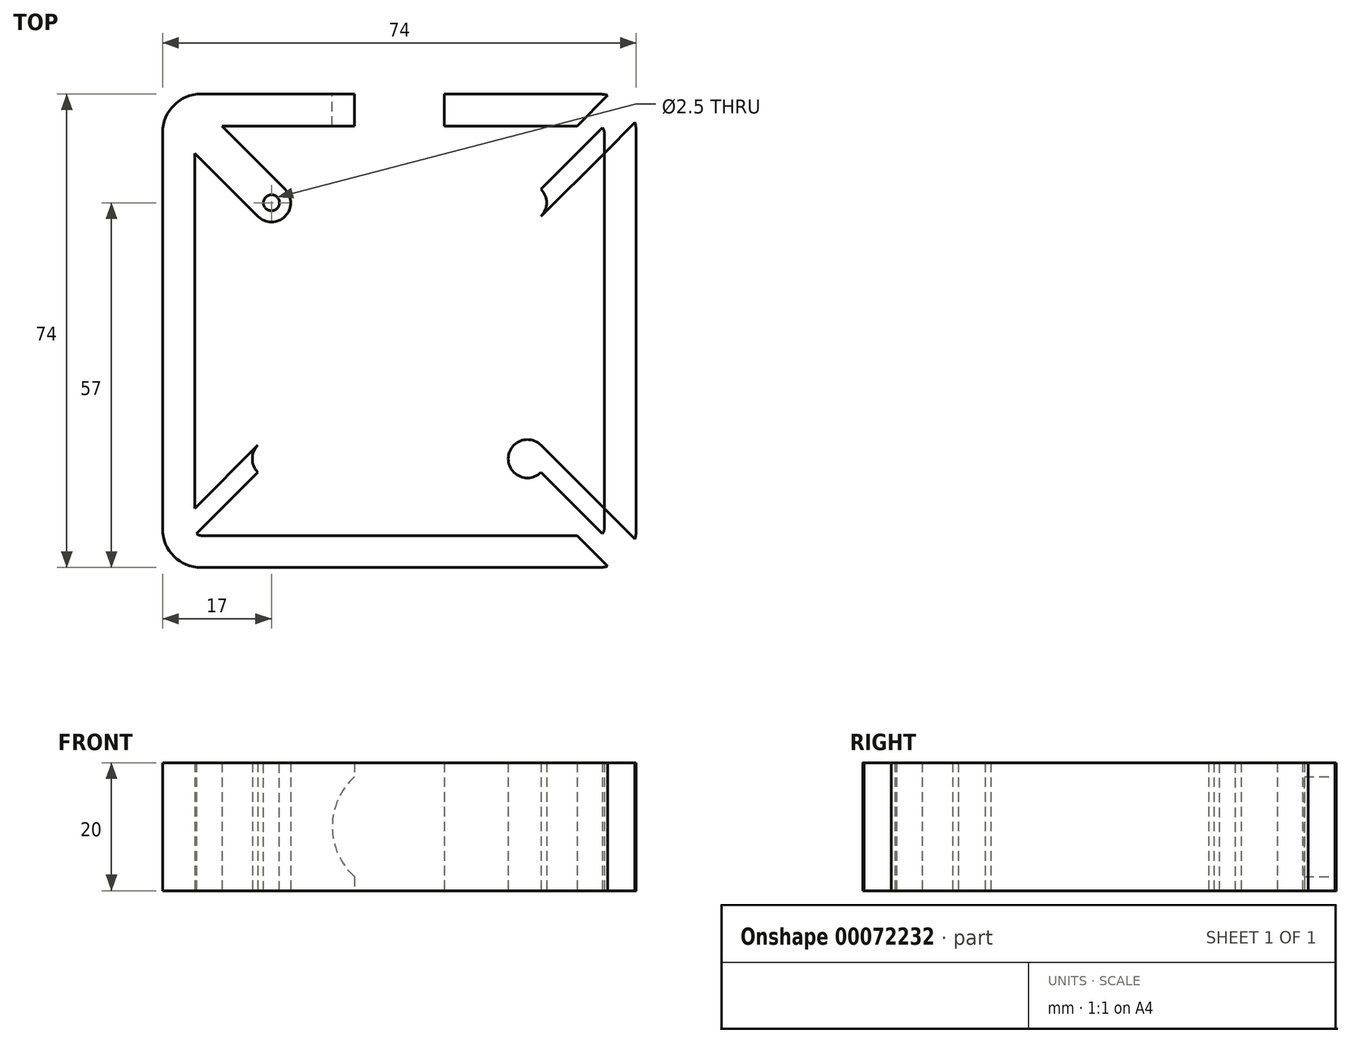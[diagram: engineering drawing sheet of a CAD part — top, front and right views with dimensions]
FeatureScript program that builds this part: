
annotation { "Feature Type Name" : "Feature", "Feature Type Description" : "" }
export const myFeature = defineFeature(function(context is Context, id is Id, definition is map)
    precondition{}
    {
        {
            var Q0;
            Q0=qCreatedBy(makeId("Top.planeOp"),FACE);
            var sketch = newSketch(context, id + "F0", { "sketchPlane" : qUnion([Q0])});
            skLineSegment(sketch, "E0.top", {"start": v(6, 74) * mm, "end": v(68, 74) * mm, "construction": true});
            skLineSegment(sketch, "E0.left", {"start": v(0, 6) * mm, "end": v(0, 68) * mm});
            skPoint(sketch, "E1.visualSharp", {"position": v(0, 74) * mm});
            skArc(sketch, "E1.filletArc", {"start": v(6, 74) * mm, "mid": v(1.76, 72.24) * mm, "end": v(0, 68) * mm});
            skPoint(sketch, "E2.visualSharp", {"position": v(0, 0) * mm});
            skArc(sketch, "E2.filletArc", {"start": v(0, 6) * mm, "mid": v(1.76, 1.76) * mm, "end": v(6, 0) * mm});
            skLineSegment(sketch, "E3", {"start": v(-6.9, 57) * mm, "end": v(40.9, 57) * mm, "construction": true});
            skLineSegment(sketch, "E4", {"start": v(37, 80.67) * mm, "end": v(37, -9.85) * mm, "construction": true});
            skLineSegment(sketch, "E5", {"start": v(30, 74) * mm, "end": v(6, 74) * mm});
            skLineSegment(sketch, "E6", {"start": v(30, 69) * mm, "end": v(30, 74) * mm});
            skLineSegment(sketch, "E7", {"start": v(37, 0) * mm, "end": v(6, 0) * mm});
            skArc(sketch, "E8.MirrorCS", {"start": v(68, 74) * mm, "mid": v(72.24, 72.24) * mm, "end": v(74, 68) * mm});
            skArc(sketch, "E9.MirrorCS", {"start": v(74, 6) * mm, "mid": v(72.24, 1.76) * mm, "end": v(68, 0) * mm});
            skLineSegment(sketch, "E10.MirrorCS", {"start": v(37, 0) * mm, "end": v(68, 0) * mm});
            skLineSegment(sketch, "E11.MirrorCS", {"start": v(44, 74) * mm, "end": v(68, 74) * mm});
            skLineSegment(sketch, "E12.MirrorCS", {"start": v(44, 69) * mm, "end": v(44, 74) * mm});
            skLineSegment(sketch, "E13.MirrorCS", {"start": v(74, 6) * mm, "end": v(74, 68) * mm});
            skLineSegment(sketch, "E14", {"start": v(6, 5) * mm, "end": v(68, 5) * mm});
            skLineSegment(sketch, "E15", {"start": v(5, 49) * mm, "end": v(5, 24.5) * mm});
            skLineSegment(sketch, "E16.MirrorCS", {"start": v(69, 49) * mm, "end": v(69, 24.5) * mm});
            skLineSegment(sketch, "E17.MirrorCS", {"start": v(68, 5) * mm, "end": v(6, 5) * mm});
            skArc(sketch, "E18.1", {"start": v(6, 69) * mm, "mid": v(5.3, 68.7) * mm, "end": v(5, 68) * mm});
            skLineSegment(sketch, "E18.2", {"start": v(5, 6) * mm, "end": v(5, 68) * mm});
            skArc(sketch, "E18.3", {"start": v(5, 6) * mm, "mid": v(5.3, 5.3) * mm, "end": v(6, 5) * mm});
            skLineSegment(sketch, "E18.4", {"start": v(37, 5) * mm, "end": v(6, 5) * mm});
            skArc(sketch, "E18.7", {"start": v(68, 69) * mm, "mid": v(68.7, 68.7) * mm, "end": v(69, 68) * mm});
            skLineSegment(sketch, "E18.8", {"start": v(69, 6) * mm, "end": v(69, 68) * mm});
            skArc(sketch, "E18.9", {"start": v(69, 6) * mm, "mid": v(68.7, 5.3) * mm, "end": v(68, 5) * mm});
            skLineSegment(sketch, "E19", {"start": v(0, 74) * mm, "end": v(17, 57) * mm});
            skLineSegment(sketch, "E20.0", {"start": v(13.18, 56.58) * mm, "end": v(14.88, 54.88) * mm});
            skLineSegment(sketch, "E21.0", {"start": v(17.42, 60.82) * mm, "end": v(19.12, 59.12) * mm});
            skCircle(sketch, "E22", {"center": v(17, 57) * mm, "radius": 3 * mm});
            skPoint(sketch, "E23", {"position": v(5, 37) * mm});
            skLineSegment(sketch, "E24", {"start": v(5, 37) * mm, "end": v(69, 37) * mm, "construction": true});
            skPoint(sketch, "E25.newPointB", {"position": v(2.12, 76.12) * mm});
            skPoint(sketch, "E26.newPointA", {"position": v(-2.12, 71.88) * mm});
            skPoint(sketch, "E26.newPointB", {"position": v(5, 68) * mm});
            skLineSegment(sketch, "E27", {"start": v(6, 69) * mm, "end": v(30, 69) * mm});
            skLineSegment(sketch, "E28", {"start": v(44, 69) * mm, "end": v(68, 69) * mm});
            skLineSegment(sketch, "E29", {"start": v(-2.12, 71.88) * mm, "end": v(14.88, 54.88) * mm});
            skLineSegment(sketch, "E30", {"start": v(19.12, 59.12) * mm, "end": v(2.12, 76.12) * mm});
            skLineSegment(sketch, "E31.MirrorCS", {"start": v(6, 5) * mm, "end": v(30, 5) * mm});
            skLineSegment(sketch, "E32.MirrorCS", {"start": v(17.42, 13.18) * mm, "end": v(19.12, 14.88) * mm});
            skLineSegment(sketch, "E33.MirrorCS", {"start": v(19.12, 14.88) * mm, "end": v(2.12, -2.12) * mm});
            skLineSegment(sketch, "E34.MirrorCS", {"start": v(0, 0) * mm, "end": v(17, 17) * mm});
            skCircle(sketch, "E35.MirrorC", {"center": v(17, 17) * mm, "radius": 3 * mm});
            skLineSegment(sketch, "E36.MirrorCS", {"start": v(-2.12, 2.12) * mm, "end": v(14.88, 19.12) * mm});
            skLineSegment(sketch, "E37.MirrorCS", {"start": v(56.58, 60.82) * mm, "end": v(54.88, 59.12) * mm});
            skLineSegment(sketch, "E38.MirrorCS", {"start": v(76.12, 71.88) * mm, "end": v(59.12, 54.88) * mm});
            skLineSegment(sketch, "E39.MirrorCS", {"start": v(74, 74) * mm, "end": v(57, 57) * mm});
            skLineSegment(sketch, "E40.MirrorCS", {"start": v(54.88, 59.12) * mm, "end": v(71.88, 76.12) * mm});
            skCircle(sketch, "E41.MirrorC", {"center": v(57, 57) * mm, "radius": 3 * mm});
            skLineSegment(sketch, "E42.MirrorCS", {"start": v(54.88, 14.88) * mm, "end": v(71.88, -2.12) * mm});
            skLineSegment(sketch, "E43.MirrorCS", {"start": v(56.58, 13.18) * mm, "end": v(54.88, 14.88) * mm});
            skLineSegment(sketch, "E44.MirrorCS", {"start": v(76.12, 2.12) * mm, "end": v(59.12, 19.12) * mm});
            skCircle(sketch, "E45.MirrorC", {"center": v(57, 17) * mm, "radius": 3 * mm});
            skLineSegment(sketch, "E46.MirrorCS", {"start": v(74, 0) * mm, "end": v(57, 17) * mm});
            skSolve(sketch);
        }
        {
            var Q0;
            {var subQ6=sQuery(id+"F0.wireOp",EDGE,"E0.left");Q0=makeQuery(id+"F0.imprint","IMPRINT",FACE,{"disambiguationData":[TD([[makeQuery(id+"F0.imprint","IMPRINT",EDGE,{"derivedFrom":subQ6}),-1.0]])]});}
            var Q1;
            {var subQ9=sQuery(id+"F0.wireOp",EDGE,"E7");Q1=makeQuery(id+"F0.imprint","IMPRINT",FACE,{"disambiguationData":[TD([[makeQuery(id+"F0.imprint","IMPRINT",EDGE,{"derivedFrom":subQ9}),-1.0]])]});}
            var Q2;
            {var subQ4=sQuery(id+"F0.wireOp",EDGE,"E5");Q2=makeQuery(id+"F0.imprint","IMPRINT",FACE,{"disambiguationData":[TD([[makeQuery(id+"F0.imprint","IMPRINT",EDGE,{"derivedFrom":subQ4}),1.0]])]});}
            var Q3;
            {var subQ4=sQuery(id+"F0.wireOp",EDGE,"E11.MirrorCS");Q3=makeQuery(id+"F0.imprint","IMPRINT",FACE,{"disambiguationData":[TD([[makeQuery(id+"F0.imprint","IMPRINT",EDGE,{"derivedFrom":subQ4}),-1.0]])]});}
            var Q4;
            {var subQ0=sQuery(id+"F0.wireOp",EDGE,"E13.MirrorCS");Q4=makeQuery(id+"F0.imprint","IMPRINT",FACE,{"disambiguationData":[TD([[makeQuery(id+"F0.imprint","IMPRINT",EDGE,{"derivedFrom":subQ0}),1.0]])]});}
            var Q5;
            {var subQ1=sQuery(id+"F0.wireOp",EDGE,"E1.filletArc");var subQ7=sQuery(id+"F0.wireOp",EDGE,"E21.0");var subQ9=makeQuery(id+"F0.imprint","INTERSECT",VERTEX,{"derivedFrom":[subQ1,subQ7]});Q5=makeQuery(id+"F0.imprint","IMPRINT",FACE,{"disambiguationData":[TD([[makeQuery(id+"F0.imprint","IMPRINT",EDGE,{"disambiguationData":[TD([[subQ9,-1.0]])],"derivedFrom":subQ1}),1.0]])]});}
            var Q6;
            {var subQ0=sQuery(id+"F0.wireOp",EDGE,"E19");var subQ1=sQuery(id+"F0.wireOp",EDGE,"E1.filletArc");var subQ2=makeQuery(id+"F0.imprint","INTERSECT",VERTEX,{"derivedFrom":[subQ1,subQ0]});Q6=makeQuery(id+"F0.imprint","IMPRINT",FACE,{"disambiguationData":[TD([[makeQuery(id+"F0.imprint","IMPRINT",EDGE,{"disambiguationData":[TD([[subQ2,-1.0]])],"derivedFrom":subQ1}),1.0]])]});}
            var Q7;
            {var subQ3=sQuery(id+"F0.wireOp",EDGE,"E18.0");var subQ7=sQuery(id+"F0.wireOp",EDGE,"E18.1");var subQ9=makeQuery(id+"F0.imprint","INTERSECT",VERTEX,{"derivedFrom":[subQ3,subQ7]});Q7=makeQuery(id+"F0.imprint","IMPRINT",FACE,{"disambiguationData":[TD([[makeQuery(id+"F0.imprint","IMPRINT",EDGE,{"disambiguationData":[TD([[subQ9,1.0]])],"derivedFrom":subQ3}),1.0]])]});}
            var Q8;
            {var subQ3=sQuery(id+"F0.wireOp",EDGE,"E18.3");var subQ7=sQuery(id+"F0.wireOp",EDGE,"E18.4");var subQ9=makeQuery(id+"F0.imprint","INTERSECT",VERTEX,{"derivedFrom":[subQ3,subQ7]});Q8=makeQuery(id+"F0.imprint","IMPRINT",FACE,{"disambiguationData":[TD([[makeQuery(id+"F0.imprint","IMPRINT",EDGE,{"disambiguationData":[TD([[subQ9,1.0]])],"derivedFrom":subQ3}),1.0]])]});}
            var Q9;
            {var subQ1=sQuery(id+"F0.wireOp",EDGE,"E2.filletArc");var subQ7=sQuery(id+"F0.wireOp",EDGE,"3a8e158c-22dd-4ffa-8a8c-b7feecd47be46.MirrorCS");var subQ9=makeQuery(id+"F0.imprint","INTERSECT",VERTEX,{"derivedFrom":[subQ1,subQ7]});Q9=makeQuery(id+"F0.imprint","IMPRINT",FACE,{"disambiguationData":[TD([[makeQuery(id+"F0.imprint","IMPRINT",EDGE,{"disambiguationData":[TD([[subQ9,-1.0]])],"derivedFrom":subQ1}),1.0]])]});}
            var Q10;
            {var subQ0=sQuery(id+"F0.wireOp",EDGE,"3a8e158c-22dd-4ffa-8a8c-b7feecd47be41.MirrorCS");var subQ1=sQuery(id+"F0.wireOp",EDGE,"E2.filletArc");var subQ2=makeQuery(id+"F0.imprint","INTERSECT",VERTEX,{"derivedFrom":[subQ1,subQ0]});Q10=makeQuery(id+"F0.imprint","IMPRINT",FACE,{"disambiguationData":[TD([[makeQuery(id+"F0.imprint","IMPRINT",EDGE,{"disambiguationData":[TD([[subQ2,-1.0]])],"derivedFrom":subQ1}),1.0]])]});}
            var Q11;
            {var subQ3=sQuery(id+"F0.wireOp",EDGE,"E18.2");var subQ5=sQuery(id+"F0.wireOp",EDGE,"E18.3");var subQ6=makeQuery(id+"F0.imprint","INTERSECT",VERTEX,{"derivedFrom":[subQ3,subQ5]});Q11=makeQuery(id+"F0.imprint","IMPRINT",FACE,{"disambiguationData":[TD([[makeQuery(id+"F0.imprint","IMPRINT",EDGE,{"disambiguationData":[TD([[subQ6,-1.0]])],"derivedFrom":subQ3}),-1.0]])]});}
            var Q12;
            {var subQ0=sQuery(id+"F0.wireOp",EDGE,"3a8e158c-22dd-4ffa-8a8c-b7feecd47be47.MirrorC");var subQ1=makeQuery(id+"F0.imprint","INTERSECT",VERTEX,{"derivedFrom":[sQuery(id+"F0.wireOp",EDGE,"3a8e158c-22dd-4ffa-8a8c-b7feecd47be45.MirrorCS"),subQ0]});Q12=makeQuery(id+"F0.imprint","IMPRINT",FACE,{"disambiguationData":[TD([[makeQuery(id+"F0.imprint","IMPRINT",EDGE,{"disambiguationData":[TD([[subQ1,-1.0]])],"derivedFrom":subQ0}),-1.0]])]});}
            var Q13;
            {var subQ3=sQuery(id+"F0.wireOp",EDGE,"E18.2");var subQ7=sQuery(id+"F0.wireOp",EDGE,"E18.1");var subQ9=makeQuery(id+"F0.imprint","INTERSECT",VERTEX,{"derivedFrom":[subQ7,subQ3]});Q13=makeQuery(id+"F0.imprint","IMPRINT",FACE,{"disambiguationData":[TD([[makeQuery(id+"F0.imprint","IMPRINT",EDGE,{"disambiguationData":[TD([[subQ9,1.0]])],"derivedFrom":subQ7}),1.0]])]});}
            var Q14;
            {var subQ0=sQuery(id+"F0.wireOp",EDGE,"E22");var subQ1=makeQuery(id+"F0.imprint","INTERSECT",VERTEX,{"derivedFrom":[sQuery(id+"F0.wireOp",EDGE,"E21.0"),subQ0]});Q14=makeQuery(id+"F0.imprint","IMPRINT",FACE,{"disambiguationData":[TD([[makeQuery(id+"F0.imprint","IMPRINT",EDGE,{"disambiguationData":[TD([[subQ1,-1.0]])],"derivedFrom":subQ0}),1.0]])]});}
            var Q15;
            {var subQ3=sQuery(id+"F0.wireOp",EDGE,"E18.7");var subQ7=sQuery(id+"F0.wireOp",EDGE,"E18.6");var subQ9=makeQuery(id+"F0.imprint","INTERSECT",VERTEX,{"derivedFrom":[subQ7,subQ3]});Q15=makeQuery(id+"F0.imprint","IMPRINT",FACE,{"disambiguationData":[TD([[makeQuery(id+"F0.imprint","IMPRINT",EDGE,{"disambiguationData":[TD([[subQ9,1.0]])],"derivedFrom":subQ7}),-1.0]])]});}
            var Q16;
            {var subQ5=sQuery(id+"F0.wireOp",EDGE,"1c03f007-1ffe-4943-b799-75a42c30466e4.MirrorCS");var subQ7=sQuery(id+"F0.wireOp",EDGE,"E8.MirrorCS");var subQ8=makeQuery(id+"F0.imprint","INTERSECT",VERTEX,{"derivedFrom":[subQ7,subQ5]});Q16=makeQuery(id+"F0.imprint","IMPRINT",FACE,{"disambiguationData":[TD([[makeQuery(id+"F0.imprint","IMPRINT",EDGE,{"disambiguationData":[TD([[subQ8,-1.0]])],"derivedFrom":subQ7}),-1.0]])]});}
            var Q17;
            {var subQ3=sQuery(id+"F0.wireOp",EDGE,"1c03f007-1ffe-4943-b799-75a42c30466e7.MirrorCS");var subQ6=sQuery(id+"F0.wireOp",EDGE,"E8.MirrorCS");var subQ9=makeQuery(id+"F0.imprint","INTERSECT",VERTEX,{"derivedFrom":[subQ6,subQ3]});Q17=makeQuery(id+"F0.imprint","IMPRINT",FACE,{"disambiguationData":[TD([[makeQuery(id+"F0.imprint","IMPRINT",EDGE,{"disambiguationData":[TD([[subQ9,-1.0]])],"derivedFrom":subQ6}),-1.0]])]});}
            var Q18;
            {var subQ3=sQuery(id+"F0.wireOp",EDGE,"E18.7");var subQ5=sQuery(id+"F0.wireOp",EDGE,"E18.8");var subQ6=makeQuery(id+"F0.imprint","INTERSECT",VERTEX,{"derivedFrom":[subQ3,subQ5]});Q18=makeQuery(id+"F0.imprint","IMPRINT",FACE,{"disambiguationData":[TD([[makeQuery(id+"F0.imprint","IMPRINT",EDGE,{"disambiguationData":[TD([[subQ6,1.0]])],"derivedFrom":subQ3}),-1.0]])]});}
            var Q19;
            {var subQ0=sQuery(id+"F0.wireOp",EDGE,"1c03f007-1ffe-4943-b799-75a42c30466e9.MirrorC");var subQ1=makeQuery(id+"F0.imprint","INTERSECT",VERTEX,{"derivedFrom":[sQuery(id+"F0.wireOp",EDGE,"1c03f007-1ffe-4943-b799-75a42c30466e4.MirrorCS"),subQ0]});Q19=makeQuery(id+"F0.imprint","IMPRINT",FACE,{"disambiguationData":[TD([[makeQuery(id+"F0.imprint","IMPRINT",EDGE,{"disambiguationData":[TD([[subQ1,-1.0]])],"derivedFrom":subQ0}),-1.0]])]});}
            var Q20;
            {var subQ0=sQuery(id+"F0.wireOp",EDGE,"7e8f61bc-852c-4eb2-8d22-d4acf16ccae015.MirrorC");var subQ1=makeQuery(id+"F0.imprint","INTERSECT",VERTEX,{"derivedFrom":[sQuery(id+"F0.wireOp",EDGE,"7e8f61bc-852c-4eb2-8d22-d4acf16ccae014.MirrorCS"),subQ0]});Q20=makeQuery(id+"F0.imprint","IMPRINT",FACE,{"disambiguationData":[TD([[makeQuery(id+"F0.imprint","IMPRINT",EDGE,{"disambiguationData":[TD([[subQ1,-1.0]])],"derivedFrom":subQ0}),1.0]])]});}
            var Q21;
            {var subQ3=sQuery(id+"F0.wireOp",EDGE,"E18.5");var subQ5=sQuery(id+"F0.wireOp",EDGE,"E18.9");var subQ6=makeQuery(id+"F0.imprint","INTERSECT",VERTEX,{"derivedFrom":[subQ3,subQ5]});Q21=makeQuery(id+"F0.imprint","IMPRINT",FACE,{"disambiguationData":[TD([[makeQuery(id+"F0.imprint","IMPRINT",EDGE,{"disambiguationData":[TD([[subQ6,1.0]])],"derivedFrom":subQ3}),1.0]])]});}
            var Q22;
            {var subQ3=sQuery(id+"F0.wireOp",EDGE,"7e8f61bc-852c-4eb2-8d22-d4acf16ccae03.MirrorCS");var subQ5=sQuery(id+"F0.wireOp",EDGE,"E9.MirrorCS");var subQ6=makeQuery(id+"F0.imprint","INTERSECT",VERTEX,{"derivedFrom":[subQ5,subQ3]});Q22=makeQuery(id+"F0.imprint","IMPRINT",FACE,{"disambiguationData":[TD([[makeQuery(id+"F0.imprint","IMPRINT",EDGE,{"disambiguationData":[TD([[subQ6,-1.0]])],"derivedFrom":subQ5}),-1.0]])]});}
            var Q23;
            {var subQ1=sQuery(id+"F0.wireOp",EDGE,"E9.MirrorCS");var subQ7=sQuery(id+"F0.wireOp",EDGE,"7e8f61bc-852c-4eb2-8d22-d4acf16ccae09.MirrorCS");var subQ9=makeQuery(id+"F0.imprint","INTERSECT",VERTEX,{"derivedFrom":[subQ1,subQ7]});Q23=makeQuery(id+"F0.imprint","IMPRINT",FACE,{"disambiguationData":[TD([[makeQuery(id+"F0.imprint","IMPRINT",EDGE,{"disambiguationData":[TD([[subQ9,-1.0]])],"derivedFrom":subQ1}),-1.0]])]});}
            var Q24;
            {var subQ3=sQuery(id+"F0.wireOp",EDGE,"E18.8");var subQ7=sQuery(id+"F0.wireOp",EDGE,"E18.9");var subQ9=makeQuery(id+"F0.imprint","INTERSECT",VERTEX,{"derivedFrom":[subQ3,subQ7]});Q24=makeQuery(id+"F0.imprint","IMPRINT",FACE,{"disambiguationData":[TD([[makeQuery(id+"F0.imprint","IMPRINT",EDGE,{"disambiguationData":[TD([[subQ9,-1.0]])],"derivedFrom":subQ3}),1.0]])]});}
            var Q25;
            {var subQ0=sQuery(id+"F0.wireOp",EDGE,"E45.MirrorC");var subQ1=makeQuery(id+"F0.imprint","INTERSECT",VERTEX,{"derivedFrom":[subQ0,sQuery(id+"F0.wireOp",EDGE,"E42.MirrorCS")]});Q25=makeQuery(id+"F0.imprint","IMPRINT",FACE,{"disambiguationData":[TD([[makeQuery(id+"F0.imprint","IMPRINT",EDGE,{"disambiguationData":[TD([[subQ1,-1.0]])],"derivedFrom":subQ0}),1.0]])]});}
            var Q26;
            {var subQ0=sQuery(id+"F0.wireOp",EDGE,"E22");var subQ1=makeQuery(id+"F0.imprint","INTERSECT",VERTEX,{"derivedFrom":[sQuery(id+"F0.wireOp",EDGE,"E30"),subQ0]});Q26=makeQuery(id+"F0.imprint","IMPRINT",FACE,{"disambiguationData":[TD([[makeQuery(id+"F0.imprint","IMPRINT",EDGE,{"disambiguationData":[TD([[subQ1,-1.0]])],"derivedFrom":subQ0}),1.0]])]});}
            var Q27;
            {var subQ0=sQuery(id+"F0.wireOp",EDGE,"E41.MirrorC");var subQ1=makeQuery(id+"F0.imprint","INTERSECT",VERTEX,{"derivedFrom":[subQ0,sQuery(id+"F0.wireOp",EDGE,"E40.MirrorCS")]});Q27=makeQuery(id+"F0.imprint","IMPRINT",FACE,{"disambiguationData":[TD([[makeQuery(id+"F0.imprint","IMPRINT",EDGE,{"disambiguationData":[TD([[subQ1,-1.0]])],"derivedFrom":subQ0}),-1.0]])]});}
            var Q28;
            {var subQ3=sQuery(id+"F0.wireOp",EDGE,"E18.1");var subQ7=sQuery(id+"F0.wireOp",EDGE,"E27");var subQ9=makeQuery(id+"F0.imprint","INTERSECT",VERTEX,{"derivedFrom":[subQ3,subQ7]});Q28=makeQuery(id+"F0.imprint","IMPRINT",FACE,{"disambiguationData":[TD([[makeQuery(id+"F0.imprint","IMPRINT",EDGE,{"disambiguationData":[TD([[subQ9,-1.0]])],"derivedFrom":subQ3}),1.0]])]});}
            var Q29;
            {var subQ0=sQuery(id+"F0.wireOp",EDGE,"E28");var subQ1=sQuery(id+"F0.wireOp",EDGE,"E18.7");var subQ2=makeQuery(id+"F0.imprint","INTERSECT",VERTEX,{"derivedFrom":[subQ1,subQ0]});Q29=makeQuery(id+"F0.imprint","IMPRINT",FACE,{"disambiguationData":[TD([[makeQuery(id+"F0.imprint","IMPRINT",EDGE,{"disambiguationData":[TD([[subQ2,-1.0]])],"derivedFrom":subQ1}),-1.0]])]});}
            var Q30;
            {var subQ0=sQuery(id+"F0.wireOp",EDGE,"E35.MirrorC");var subQ1=makeQuery(id+"F0.imprint","INTERSECT",VERTEX,{"derivedFrom":[subQ0,sQuery(id+"F0.wireOp",EDGE,"E33.MirrorCS")]});Q30=makeQuery(id+"F0.imprint","IMPRINT",FACE,{"disambiguationData":[TD([[makeQuery(id+"F0.imprint","IMPRINT",EDGE,{"disambiguationData":[TD([[subQ1,-1.0]])],"derivedFrom":subQ0}),-1.0]])]});}
            var Q31;
            {var subQ3=sQuery(id+"F0.wireOp",EDGE,"E17.MirrorCS");var subQ7=sQuery(id+"F0.wireOp",EDGE,"E18.9");var subQ8=makeQuery(id+"F0.imprint","INTERSECT",VERTEX,{"derivedFrom":[subQ3,subQ7]});Q31=makeQuery(id+"F0.imprint","IMPRINT",FACE,{"disambiguationData":[TD([[makeQuery(id+"F0.imprint","IMPRINT",EDGE,{"disambiguationData":[TD([[subQ8,-1.0]])],"derivedFrom":subQ3}),-1.0]])]});}
            extrude(context, id + "F1", {"entities" : qUnion([Q0, Q1, Q2, Q3, Q4, Q5, Q6, Q7, Q8, Q9, Q10, Q11, Q12, Q13, Q14, Q15, Q16, Q17, Q18, Q19, Q20, Q21, Q22, Q23, Q24, Q25, Q26, Q27, Q28, Q29, Q30, Q31]), "depth" : 20 * mm});
        }
        {
            var Q0;
            Q0=makeQuery(id+"F1.opExtrude","SWEPT_FACE",FACE,{"disambiguationData":[OSD([sQuery(id+"F0.wireOp",EDGE,"E11.MirrorCS")])]});
            var sketch = newSketch(context, id + "F2", { "sketchPlane" : qUnion([Q0])});
            skLineSegment(sketch, "E47", {"start": v(-68, 10) * mm, "end": v(-6, 10) * mm});
            skPoint(sketch, "E47.endSnap0", {"position": v(-68, 10) * mm});
            skCircle(sketch, "E48", {"center": v(-37, 10) * mm, "radius": 10.5 * mm});
            skSolve(sketch);
        }
        {
            var Q0;
            Q0=qSketchRegion(id+"F2",true);
            extrude(context, id + "F3", {"entities" : qUnion([Q0]), "oppositeDirection" : true, "depth" : 25 * mm});
        }
        {
            var Q0;
            Q0=makeQuery(id+"F3.opExtrude","SWEPT_BODY",BODY,{"disambiguationData":[OSD([sQuery(id+"F2.wireOp",EDGE,"E48")])]});
            var Q1;
            Q1=makeQuery(id+"F1.opExtrude","SWEPT_BODY",BODY,{"disambiguationData":[OSD([sQuery(id+"F0.wireOp",EDGE,"E0.left"),sQuery(id+"F0.wireOp",EDGE,"E1.filletArc"),sQuery(id+"F0.wireOp",EDGE,"E2.filletArc"),sQuery(id+"F0.wireOp",EDGE,"Cqtl8sYd-x8eA-p0Ci-qh9f-KP0X5arBush6"),sQuery(id+"F0.wireOp",EDGE,"t0FDsQM7-GWqa-ov0J-h6zA-vYq5VfIPqZyT"),sQuery(id+"F0.wireOp",EDGE,"dZylRY6x-1Ij4-8kdU-HT9k-4JOX3FaVU0Y9"),sQuery(id+"F0.wireOp",EDGE,"j7dCo05Q-NK8S-PAB8-5yVi-hLkRdOoC1qtI"),sQuery(id+"F0.wireOp",EDGE,"QDbTKYnb-cyUq-QaIH-Lbgu-o2sDgkH0uhrb"),sQuery(id+"F0.wireOp",EDGE,"E5"),sQuery(id+"F0.wireOp",EDGE,"7Z1dPvrn-90ga-fMmc-oZWn-hNLnTgOSiSnF"),sQuery(id+"F0.wireOp",EDGE,"iqIQcJiS-4jgR-Reb2-r4IF-rO4RF3F6gWLn"),sQuery(id+"F0.wireOp",EDGE,"E6"),sQuery(id+"F0.wireOp",EDGE,"E7"),sQuery(id+"F0.wireOp",EDGE,"zJ4gfM54-7Wjp-qNnH-eqyB-9P3vSi8HfcG8"),sQuery(id+"F0.wireOp",EDGE,"abba0434-76aa-401e-ba99-632714cfb67c0.MirrorCS"),sQuery(id+"F0.wireOp",EDGE,"E8.MirrorCS"),sQuery(id+"F0.wireOp",EDGE,"abba0434-76aa-401e-ba99-632714cfb67c3.MirrorCS"),sQuery(id+"F0.wireOp",EDGE,"E9.MirrorCS"),sQuery(id+"F0.wireOp",EDGE,"abba0434-76aa-401e-ba99-632714cfb67c6.MirrorCS"),sQuery(id+"F0.wireOp",EDGE,"E10.MirrorCS"),sQuery(id+"F0.wireOp",EDGE,"E11.MirrorCS"),sQuery(id+"F0.wireOp",EDGE,"E12.MirrorCS"),sQuery(id+"F0.wireOp",EDGE,"abba0434-76aa-401e-ba99-632714cfb67c10.MirrorCS"),sQuery(id+"F0.wireOp",EDGE,"abba0434-76aa-401e-ba99-632714cfb67c12.MirrorCS"),sQuery(id+"F0.wireOp",EDGE,"abba0434-76aa-401e-ba99-632714cfb67c14.MirrorCS"),sQuery(id+"F0.wireOp",EDGE,"abba0434-76aa-401e-ba99-632714cfb67c15.MirrorCS"),sQuery(id+"F0.wireOp",EDGE,"abba0434-76aa-401e-ba99-632714cfb67c16.MirrorCS"),sQuery(id+"F0.wireOp",EDGE,"E13.MirrorCS")])]});
            booleanBodies(context, id + "F4", {"operationType" : BooleanOperationType.SUBTRACTION, "tools" : qUnion([Q0]), "targets" : qUnion([Q1])});
        }
        {
            var Q0;
            Q0=makeQuery(id+"F1.opExtrude","CAP_FACE",FACE,{"disambiguationData":[OSD([sQuery(id+"F0.wireOp",EDGE,"E0.left"),sQuery(id+"F0.wireOp",EDGE,"E1.filletArc"),sQuery(id+"F0.wireOp",EDGE,"E2.filletArc"),sQuery(id+"F0.wireOp",EDGE,"E5"),sQuery(id+"F0.wireOp",EDGE,"7Z1dPvrn-90ga-fMmc-oZWn-hNLnTgOSiSnF"),sQuery(id+"F0.wireOp",EDGE,"E6"),sQuery(id+"F0.wireOp",EDGE,"E7"),sQuery(id+"F0.wireOp",EDGE,"abba0434-76aa-401e-ba99-632714cfb67c0.MirrorCS"),sQuery(id+"F0.wireOp",EDGE,"E8.MirrorCS"),sQuery(id+"F0.wireOp",EDGE,"E9.MirrorCS"),sQuery(id+"F0.wireOp",EDGE,"E10.MirrorCS"),sQuery(id+"F0.wireOp",EDGE,"E11.MirrorCS"),sQuery(id+"F0.wireOp",EDGE,"E12.MirrorCS"),sQuery(id+"F0.wireOp",EDGE,"E13.MirrorCS"),sQuery(id+"F0.wireOp",EDGE,"im5txOst-8Odg-fi4W-FYaJ-8ID1UmsptdEB"),sQuery(id+"F0.wireOp",EDGE,"lcC4UBLz-14uk-YhWL-JcjU-0Uq4AyqIm3Wz"),sQuery(id+"F0.wireOp",EDGE,"4N9wEozH-rKxY-teKg-d8K6-DSi5X649WLBI"),sQuery(id+"F0.wireOp",EDGE,"E15"),sQuery(id+"F0.wireOp",EDGE,"F7DgLbcL-pQL6-zkUl-6RKA-MosChOAkBqvI"),sQuery(id+"F0.wireOp",EDGE,"x9N6SBtd-BwRt-ljrM-5wA8-Nc5sFgZOK0xx"),sQuery(id+"F0.wireOp",EDGE,"SL2UcdPw-Ifz9-xt5r-vjnY-sPrOThKhgMED"),sQuery(id+"F0.wireOp",EDGE,"5f8056d6-9bf9-4eda-85d3-c9ba6db090ec0.MirrorCS"),sQuery(id+"F0.wireOp",EDGE,"5f8056d6-9bf9-4eda-85d3-c9ba6db090ec1.MirrorCS"),sQuery(id+"F0.wireOp",EDGE,"5f8056d6-9bf9-4eda-85d3-c9ba6db090ec2.MirrorCS"),sQuery(id+"F0.wireOp",EDGE,"E16.MirrorCS"),sQuery(id+"F0.wireOp",EDGE,"5f8056d6-9bf9-4eda-85d3-c9ba6db090ec4.MirrorCS"),sQuery(id+"F0.wireOp",EDGE,"5f8056d6-9bf9-4eda-85d3-c9ba6db090ec5.MirrorCS"),sQuery(id+"F0.wireOp",EDGE,"5f8056d6-9bf9-4eda-85d3-c9ba6db090ec6.MirrorCS"),sQuery(id+"F0.wireOp",EDGE,"E17.MirrorCS")])],"isStart":false});
            var sketch = newSketch(context, id + "F5", { "sketchPlane" : qUnion([Q0])});
            skPoint(sketch, "E49", {"position": v(57, 57) * mm});
            skPoint(sketch, "E50", {"position": v(17, 57) * mm});
            skPoint(sketch, "E51", {"position": v(17, 17) * mm});
            skPoint(sketch, "E52", {"position": v(57, 17) * mm});
            skSolve(sketch);
        }
        {
            var Q0;
            Q0=sQuery(id+"F5.wireOp",VERTEX,"E50");
            var Q1;
            Q1=sQuery(id+"F5.wireOp",VERTEX,"E49");
            var Q2;
            Q2=sQuery(id+"F5.wireOp",VERTEX,"E52");
            var Q3;
            Q3=sQuery(id+"F5.wireOp",VERTEX,"E51");
            var Q4;
            Q4=makeQuery(id+"F1.opExtrude","SWEPT_BODY",BODY,{"disambiguationData":[OSD([sQuery(id+"F0.wireOp",EDGE,"E0.left"),sQuery(id+"F0.wireOp",EDGE,"E1.filletArc"),sQuery(id+"F0.wireOp",EDGE,"E2.filletArc"),sQuery(id+"F0.wireOp",EDGE,"E5"),sQuery(id+"F0.wireOp",EDGE,"7Z1dPvrn-90ga-fMmc-oZWn-hNLnTgOSiSnF"),sQuery(id+"F0.wireOp",EDGE,"E6"),sQuery(id+"F0.wireOp",EDGE,"E7"),sQuery(id+"F0.wireOp",EDGE,"abba0434-76aa-401e-ba99-632714cfb67c0.MirrorCS"),sQuery(id+"F0.wireOp",EDGE,"E8.MirrorCS"),sQuery(id+"F0.wireOp",EDGE,"E9.MirrorCS"),sQuery(id+"F0.wireOp",EDGE,"E10.MirrorCS"),sQuery(id+"F0.wireOp",EDGE,"E11.MirrorCS"),sQuery(id+"F0.wireOp",EDGE,"E12.MirrorCS"),sQuery(id+"F0.wireOp",EDGE,"E13.MirrorCS"),sQuery(id+"F0.wireOp",EDGE,"im5txOst-8Odg-fi4W-FYaJ-8ID1UmsptdEB"),sQuery(id+"F0.wireOp",EDGE,"lcC4UBLz-14uk-YhWL-JcjU-0Uq4AyqIm3Wz"),sQuery(id+"F0.wireOp",EDGE,"4N9wEozH-rKxY-teKg-d8K6-DSi5X649WLBI"),sQuery(id+"F0.wireOp",EDGE,"E15"),sQuery(id+"F0.wireOp",EDGE,"F7DgLbcL-pQL6-zkUl-6RKA-MosChOAkBqvI"),sQuery(id+"F0.wireOp",EDGE,"x9N6SBtd-BwRt-ljrM-5wA8-Nc5sFgZOK0xx"),sQuery(id+"F0.wireOp",EDGE,"SL2UcdPw-Ifz9-xt5r-vjnY-sPrOThKhgMED"),sQuery(id+"F0.wireOp",EDGE,"5f8056d6-9bf9-4eda-85d3-c9ba6db090ec0.MirrorCS"),sQuery(id+"F0.wireOp",EDGE,"5f8056d6-9bf9-4eda-85d3-c9ba6db090ec1.MirrorCS"),sQuery(id+"F0.wireOp",EDGE,"5f8056d6-9bf9-4eda-85d3-c9ba6db090ec2.MirrorCS"),sQuery(id+"F0.wireOp",EDGE,"E16.MirrorCS"),sQuery(id+"F0.wireOp",EDGE,"5f8056d6-9bf9-4eda-85d3-c9ba6db090ec4.MirrorCS"),sQuery(id+"F0.wireOp",EDGE,"5f8056d6-9bf9-4eda-85d3-c9ba6db090ec5.MirrorCS"),sQuery(id+"F0.wireOp",EDGE,"5f8056d6-9bf9-4eda-85d3-c9ba6db090ec6.MirrorCS"),sQuery(id+"F0.wireOp",EDGE,"E17.MirrorCS")])]});
            hole(context, id + "F6", {"style" : HoleStyle.SIMPLE, "endStyle" : HoleEndStyle.THROUGH, "holeDiameter" : 2.5 * mm, "locations" : qUnion([Q0, Q1, Q2, Q3]), "scope" : qUnion([Q4]), "isTappedThrough" : true});
        }
    });
